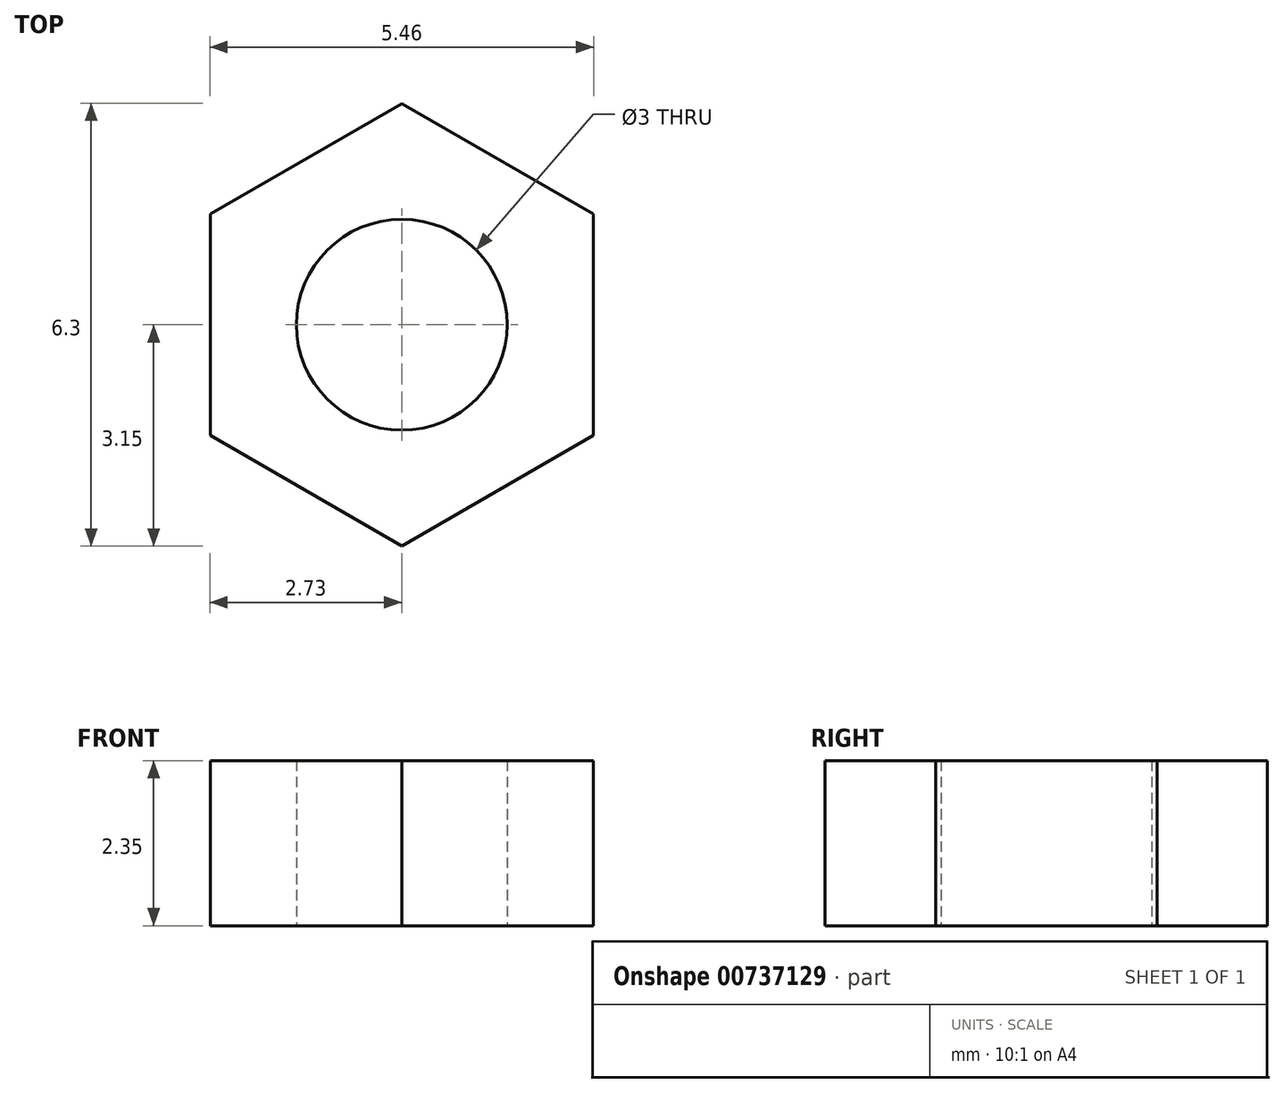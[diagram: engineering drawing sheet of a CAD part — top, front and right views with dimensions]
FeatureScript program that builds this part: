
annotation { "Feature Type Name" : "Feature", "Feature Type Description" : "" }
export const myFeature = defineFeature(function(context is Context, id is Id, definition is map)
    precondition{}
    {
        {
            var Q0;
            Q0=qCreatedBy(makeId("Top.planeOp"),FACE);
            var sketch = newSketch(context, id + "F0", { "sketchPlane" : qUnion([Q0])});
            skCircle(sketch, "E0.cCircle", {"center": v(0, 0) * mm, "radius": 2.73 * mm, "construction": true});
            skLineSegment(sketch, "E0.0", {"start": v(2.73, 1.57) * mm, "end": v(2.73, -1.57) * mm});
            skLineSegment(sketch, "E0.1", {"start": v(2.73, -1.57) * mm, "end": v(0, -3.15) * mm});
            skLineSegment(sketch, "E0.2", {"start": v(0, -3.15) * mm, "end": v(-2.73, -1.57) * mm});
            skLineSegment(sketch, "E0.3", {"start": v(-2.73, -1.57) * mm, "end": v(-2.73, 1.57) * mm});
            skLineSegment(sketch, "E0.4", {"start": v(-2.73, 1.57) * mm, "end": v(0, 3.15) * mm});
            skLineSegment(sketch, "E0.5", {"start": v(0, 3.15) * mm, "end": v(2.73, 1.57) * mm});
            skPoint(sketch, "E0.0.midPoint", {"position": v(2.73, 0) * mm});
            skCircle(sketch, "E1", {"center": v(0, 0) * mm, "radius": 1.5 * mm});
            skLineSegment(sketch, "E2", {"start": v(-2.73, 1.57) * mm, "end": v(2.73, 1.57) * mm, "construction": true});
            skSolve(sketch);
        }
        {
            var Q0;
            Q0=makeQuery(id+"F0.imprint","IMPRINT",FACE,{"disambiguationData":[TD([[makeQuery(id+"F0.imprint","IMPRINT",EDGE,{"derivedFrom":sQuery(id+"F0.wireOp",EDGE,"E0.0")}),-1.0]])]});
            extrude(context, id + "F1", {"entities" : qUnion([Q0]), "depth" : 2.35 * mm, "offsetDistance" : 25 * mm});
        }
    });
